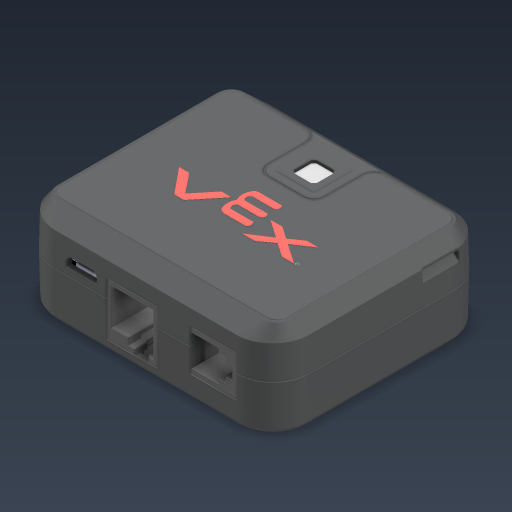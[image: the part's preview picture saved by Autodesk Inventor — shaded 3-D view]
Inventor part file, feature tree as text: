
AUTODESK INVENTOR PART (.ipt)
format: ipt  version: 2023 (Build 270158000, 158)  size: 12,648,960 bytes
history: native  units: in
note: dims shown in document units (in); Inventor stores cm internally (conversion verified against a paired STEP export)
features: other x19, thread x2, extrude x1, sketch x1
ambient origin geometry x8: Origin, YZ Plane, XZ Plane, XY Plane, X Axis, Y Axis, Z Axis, Center Point
bodies: Solid1 (feature_tree), Solid2 (feature_tree), Solid3 (feature_tree), Solid4 (feature_tree), Solid5 (feature_tree), Solid6 (feature_tree), Solid7 (feature_tree), Solid8 (feature_tree), Solid9 (feature_tree), Solid10 (feature_tree), Solid11 (feature_tree), Solid12 (feature_tree), Solid13 (feature_tree), Solid14 (feature_tree), Solid15 (feature_tree), Solid16 (feature_tree), Solid17 (feature_tree), Solid18 (feature_tree), Solid19 (feature_tree)
feature tree (23):
  extrude  "Extrusion1"  TaperAngle=0.0deg  [1 undecoded]
  thread  "Thread1"  [1 undecoded]
  thread  "Thread2"  [1 undecoded]
  sketch  "Sketch1"  dims[d0=0.0in d1=0.0in d20=0.002in d21=0.0in d23=0.3937in d24=0.0in d25=0.3937in d26=0.0in]
  other  "276-4850-001 Rev17_1:1"
  other  "276-4850-002 Rev30_2:1"
  other  "276-4850-002 Rev30_2:2"
  other  "276-4850-002 Rev30_2:3"
  other  "276-4850-902 Rev1_14:1"
  other  "276-4810-907 Rev1_15:1"
  other  "SAV8507O_Assembled and Stuck Down_16:1"
  other  "276-4831-004 Rev1_17:1"
  other  "USB205FB-C1014205_18:1"
  other  "276-4850-004 Rev8_4:1"
  other  "276-4850-003 Rev5_5:1"
  other  "276-4850-005 Rev6_6:1"
  other  "228-2530-013 Rev20_7:1"
  other  "228-2530-013 Rev20_8:1"
  other  "276-4850-013 Rev3_9:1"
  other  "276-4850-015 Rev2_10:1"
  other  "276-4850-015 Rev2_11:1"
  other  "276-4850-018 Rev2_12:1"
  other  "276-4850-018 Rev2_13:1"
note: 3 required parameter values undecoded (feature->parameter linkage not recoverable at this tier; creation-order binding heuristic only, values carry confidence <= 0.55)
